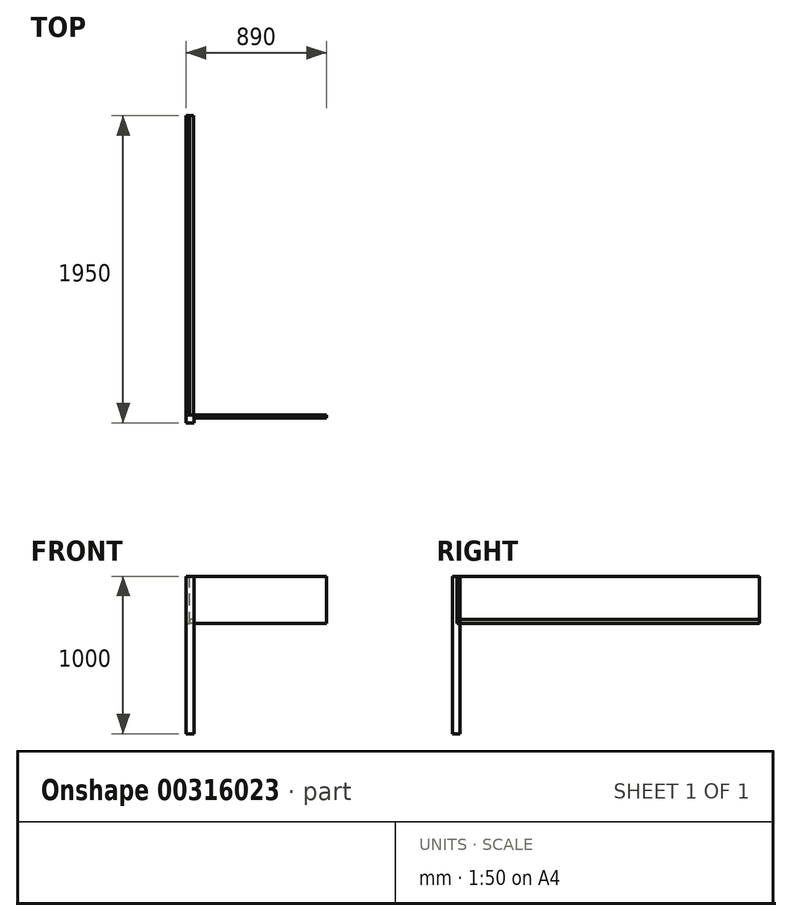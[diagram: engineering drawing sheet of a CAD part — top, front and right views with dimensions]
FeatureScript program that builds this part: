
annotation { "Feature Type Name" : "Feature", "Feature Type Description" : "" }
export const myFeature = defineFeature(function(context is Context, id is Id, definition is map)
    precondition{}
    {
        {
            var Q0;
            Q0=qCreatedBy(makeId("Front.planeOp"),FACE);
            var sketch = newSketch(context, id + "F0", { "sketchPlane" : qUnion([Q0])});
            skLineSegment(sketch, "E0.bottom", {"start": v(0, 0) * mm, "end": v(20, 0) * mm});
            skLineSegment(sketch, "E0.top", {"start": v(0, 300) * mm, "end": v(20, 300) * mm});
            skLineSegment(sketch, "E0.left", {"start": v(0, 0) * mm, "end": v(0, 300) * mm});
            skLineSegment(sketch, "E0.right", {"start": v(20, 0) * mm, "end": v(20, 300) * mm});
            skSolve(sketch);
        }
        {
            var Q0;
            Q0=qSketchRegion(id+"F0",true);
            extrude(context, id + "F1", {"entities" : qUnion([Q0]), "depth" : 1900 * mm});
        }
        {
            var Q0;
            Q0=makeQuery(id+"F1.opExtrude","CAP_FACE",FACE,{"disambiguationData":[OSD([sQuery(id+"F0.wireOp",EDGE,"E0.bottom"),sQuery(id+"F0.wireOp",EDGE,"E0.top"),sQuery(id+"F0.wireOp",EDGE,"E0.left"),sQuery(id+"F0.wireOp",EDGE,"E0.right")])],"isStart":false});
            var sketch = newSketch(context, id + "F2", { "sketchPlane" : qUnion([Q0])});
            skLineSegment(sketch, "E1.bottom", {"start": v(20, 0) * mm, "end": v(45, 0) * mm});
            skLineSegment(sketch, "E1.top", {"start": v(20, 25) * mm, "end": v(45, 25) * mm});
            skLineSegment(sketch, "E1.left", {"start": v(20, 0) * mm, "end": v(20, 25) * mm});
            skLineSegment(sketch, "E1.right", {"start": v(45, 0) * mm, "end": v(45, 25) * mm});
            skSolve(sketch);
        }
        {
            var Q0;
            Q0=makeQuery(id+"F2.imprint","IMPRINT",FACE,{"disambiguationData":[TD([[makeQuery(id+"F2.imprint","IMPRINT",EDGE,{"derivedFrom":sQuery(id+"F2.wireOp",EDGE,"E1.bottom")}),1.0]])]});
            var Q1;
            Q1=makeQuery(id+"F1.opExtrude","CAP_FACE",FACE,{"disambiguationData":[OSD([sQuery(id+"F0.wireOp",EDGE,"E0.bottom"),sQuery(id+"F0.wireOp",EDGE,"E0.top"),sQuery(id+"F0.wireOp",EDGE,"E0.left"),sQuery(id+"F0.wireOp",EDGE,"E0.right")])],"isStart":true});
            extrude(context, id + "F3", {"entities" : qUnion([Q0]), "endBound" : BoundingType.UP_TO_SURFACE, "oppositeDirection" : true, "endBoundEntityFace" : qUnion([Q1]), "depth" : 25 * mm});
        }
        {
            var Q0;
            Q0=makeQuery(id+"F1.opExtrude","SWEPT_FACE",FACE,{"disambiguationData":[OSD([sQuery(id+"F0.wireOp",EDGE,"E0.top")])]});
            var sketch = newSketch(context, id + "F4", { "sketchPlane" : qUnion([Q0])});
            skLineSegment(sketch, "E2.bottom", {"start": v(0, -1900) * mm, "end": v(50, -1900) * mm});
            skLineSegment(sketch, "E2.top", {"start": v(0, -1950) * mm, "end": v(50, -1950) * mm});
            skLineSegment(sketch, "E2.left", {"start": v(0, -1900) * mm, "end": v(0, -1950) * mm});
            skLineSegment(sketch, "E2.right", {"start": v(50, -1900) * mm, "end": v(50, -1950) * mm});
            skSolve(sketch);
        }
        {
            var Q0;
            Q0=qSketchRegion(id+"F4",true);
            extrude(context, id + "F5", {"entities" : qUnion([Q0]), "oppositeDirection" : true, "depth" : 1000 * mm});
        }
        {
            var Q0;
            Q0=makeQuery(id+"F5.opExtrude","SWEPT_BODY",BODY,{"disambiguationData":[OSD([sQuery(id+"F4.wireOp",EDGE,"E2.bottom"),sQuery(id+"F4.wireOp",EDGE,"E2.top"),sQuery(id+"F4.wireOp",EDGE,"E2.left"),sQuery(id+"F4.wireOp",EDGE,"E2.right")])]});
            transform(context, id + "F6", {"entities" : qUnion([Q0]), "transformType" : TransformType.TRANSLATION_3D, "dx" : 0 * mm, "dy" : 0 * mm, "dz" : 0 * mm, "makeCopy" : true});
        }
        {
            var Q0;
            Q0=makeQuery(id+"F6.opPattern","COPY",BODY,{"derivedFrom":makeQuery(id+"F5.opExtrude","SWEPT_BODY",BODY,{"disambiguationData":[OSD([sQuery(id+"F4.wireOp",EDGE,"E2.bottom"),sQuery(id+"F4.wireOp",EDGE,"E2.top"),sQuery(id+"F4.wireOp",EDGE,"E2.left"),sQuery(id+"F4.wireOp",EDGE,"E2.right")])]}),"instanceName":"1"});
            deleteBodies(context, id + "F7", {"entities" : qUnion([Q0])});
        }
        {
            var Q0;
            Q0=makeQuery(id+"F5.opExtrude","SWEPT_FACE",FACE,{"disambiguationData":[OSD([sQuery(id+"F4.wireOp",EDGE,"E2.right")])]});
            var sketch = newSketch(context, id + "F8", { "sketchPlane" : qUnion([Q0])});
            skLineSegment(sketch, "E3.bottom", {"start": v(-1900, 300) * mm, "end": v(-1920, 300) * mm});
            skLineSegment(sketch, "E3.top", {"start": v(-1900, 0) * mm, "end": v(-1920, 0) * mm});
            skLineSegment(sketch, "E3.left", {"start": v(-1900, 300) * mm, "end": v(-1900, 0) * mm});
            skLineSegment(sketch, "E3.right", {"start": v(-1920, 300) * mm, "end": v(-1920, 0) * mm});
            skSolve(sketch);
        }
        {
            var Q0;
            Q0=makeQuery(id+"F8.imprint","IMPRINT",FACE,{"disambiguationData":[TD([[makeQuery(id+"F8.imprint","IMPRINT",EDGE,{"derivedFrom":sQuery(id+"F8.wireOp",EDGE,"E3.bottom")}),1.0]])]});
            extrude(context, id + "F9", {"entities" : qUnion([Q0]), "depth" : 840 * mm});
        }
    });
